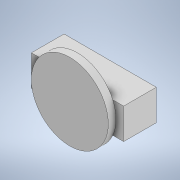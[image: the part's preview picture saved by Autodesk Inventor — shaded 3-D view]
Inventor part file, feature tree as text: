
AUTODESK INVENTOR PART (.ipt)
format: ipt  version: 2020.1 (Build 241239000, 239)  size: 111,616 bytes
history: native  units: mm
features: extrude x2, sketch x2
ambient origin geometry x8: Origin, YZ Plane, XZ Plane, XY Plane, X Axis, Y Axis, Z Axis, Center Point
bodies: Solid1 (feature_tree)
feature tree (4):
  extrude  "Extrusion1"  Depth=4.0mm
  extrude  "Extrusion3"  Depth=10.0mm
  sketch  "Sketch1"  dims[d2=2.0mm d3=4.0mm]
  sketch  "Sketch2"  dims[d4=4.25mm d5=0.0mm d9=10.0mm d10=1.0mm d11=0.0mm]
